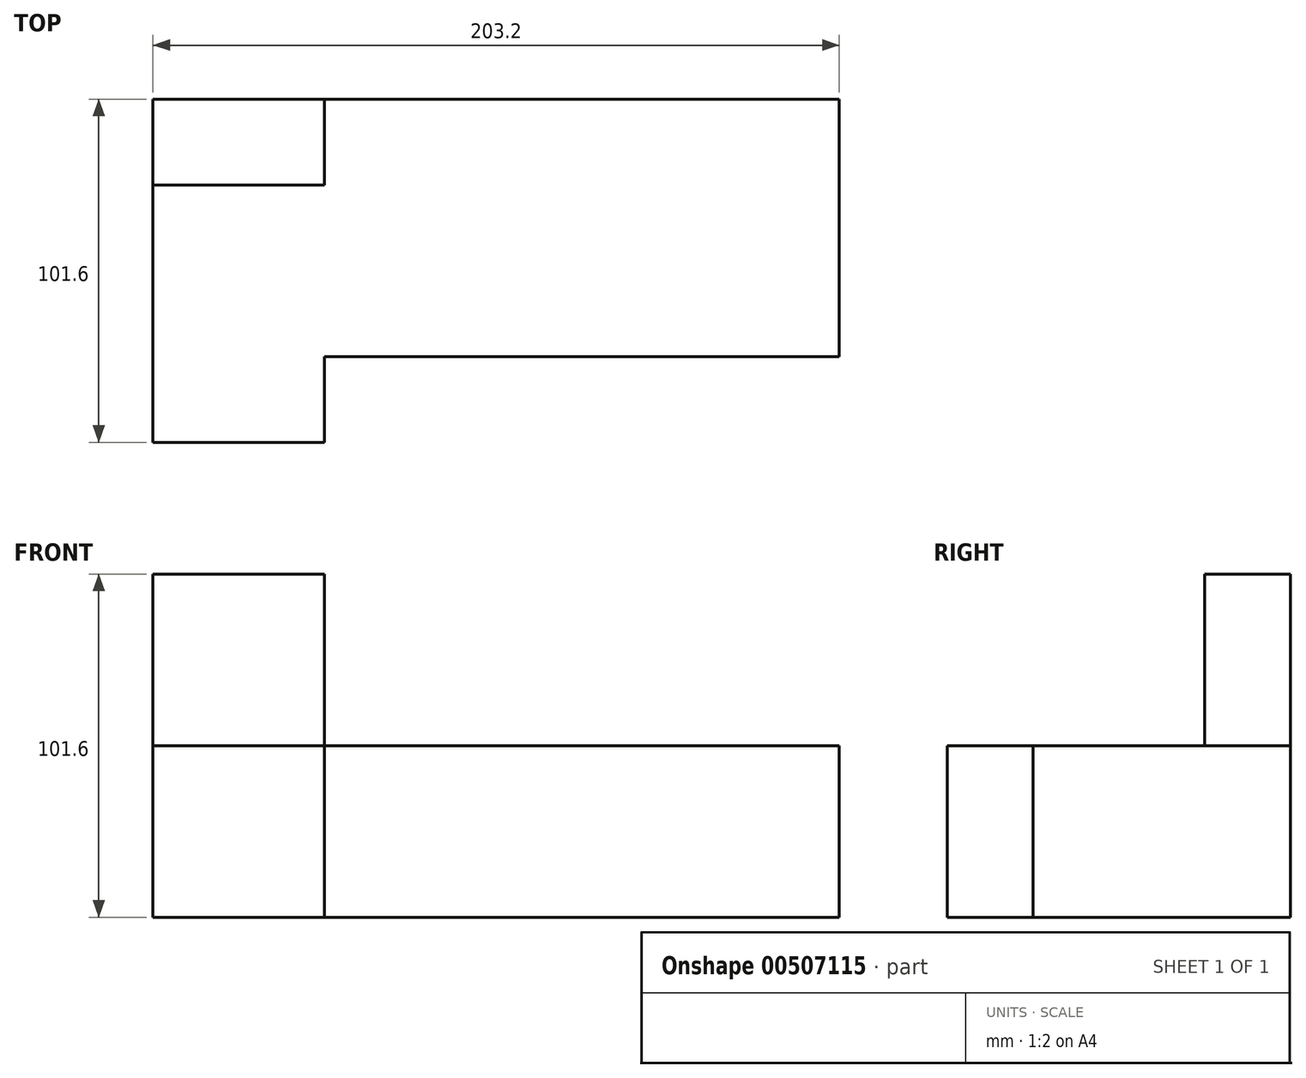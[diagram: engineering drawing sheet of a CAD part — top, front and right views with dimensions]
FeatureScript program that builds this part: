
annotation { "Feature Type Name" : "Feature", "Feature Type Description" : "" }
export const myFeature = defineFeature(function(context is Context, id is Id, definition is map)
    precondition{}
    {
        {
            var Q0;
            Q0=qCreatedBy(makeId("Top.planeOp"),FACE);
            var sketch = newSketch(context, id + "F0", { "sketchPlane" : qUnion([Q0])});
            skLineSegment(sketch, "E0.bottom", {"start": v(101.6, 50.8) * mm, "end": v(-101.6, 50.8) * mm});
            skLineSegment(sketch, "E0.top", {"start": v(101.6, -50.8) * mm, "end": v(-101.6, -50.8) * mm});
            skLineSegment(sketch, "E0.left", {"start": v(101.6, 50.8) * mm, "end": v(101.6, -50.8) * mm});
            skLineSegment(sketch, "E0.right", {"start": v(-101.6, 50.8) * mm, "end": v(-101.6, -50.8) * mm});
            skPoint(sketch, "E0.middle", {"position": v(0, 0) * mm});
            skSolve(sketch);
        }
        {
            var Q0;
            Q0 = qSketchRegion(id + "F0", true);
            extrude(context, id + "F1", {"entities" : qUnion([Q0]), "depth" : 50.8 * mm});
        }
        {
            var Q0;
            Q0=makeQuery(id+"F1.opExtrude","CAP_FACE",FACE,{"disambiguationData":[OSD([sQuery(id+"F0.wireOp",EDGE,"E0.bottom"),sQuery(id+"F0.wireOp",EDGE,"E0.top"),sQuery(id+"F0.wireOp",EDGE,"E0.left"),sQuery(id+"F0.wireOp",EDGE,"E0.right")])],"isStart":false});
            var sketch = newSketch(context, id + "F2", { "sketchPlane" : qUnion([Q0])});
            skLineSegment(sketch, "E1.bottom", {"start": v(101.6, -50.8) * mm, "end": v(-50.8, -50.8) * mm});
            skLineSegment(sketch, "E1.top", {"start": v(101.6, -25.4) * mm, "end": v(-50.8, -25.4) * mm});
            skLineSegment(sketch, "E1.left", {"start": v(101.6, -50.8) * mm, "end": v(101.6, -25.4) * mm});
            skLineSegment(sketch, "E1.right", {"start": v(-50.8, -50.8) * mm, "end": v(-50.8, -25.4) * mm});
            skSolve(sketch);
        }
        {
            var Q0;
            Q0 = qSketchRegion(id + "F2", true);
            var Q1;
            Q1=makeQuery(id+"F2.imprint","IMPRINT",FACE,{"disambiguationData":[TD([[makeQuery(id+"F2.imprint","IMPRINT",EDGE,{"derivedFrom":sQuery(id+"F2.wireOp",EDGE,"E1.bottom")}),-1.0]])]});
            extrude(context, id + "F3", {"entities" : qUnion([Q0, Q1]), "operationType" : NewBodyOperationType.REMOVE, "oppositeDirection" : true, "depth" : 50.8 * mm});
        }
        {
            var Q0;
            Q0=makeQuery(id+"F1.opExtrude","CAP_FACE",FACE,{"disambiguationData":[OSD([sQuery(id+"F0.wireOp",EDGE,"E0.bottom"),sQuery(id+"F0.wireOp",EDGE,"E0.top"),sQuery(id+"F0.wireOp",EDGE,"E0.left"),sQuery(id+"F0.wireOp",EDGE,"E0.right")])],"isStart":false});
            var sketch = newSketch(context, id + "F4", { "sketchPlane" : qUnion([Q0])});
            skLineSegment(sketch, "E2.bottom", {"start": v(-101.6, 50.8) * mm, "end": v(-50.8, 50.8) * mm});
            skLineSegment(sketch, "E2.top", {"start": v(-101.6, 25.4) * mm, "end": v(-50.8, 25.4) * mm});
            skLineSegment(sketch, "E2.left", {"start": v(-101.6, 50.8) * mm, "end": v(-101.6, 25.4) * mm});
            skLineSegment(sketch, "E2.right", {"start": v(-50.8, 50.8) * mm, "end": v(-50.8, 25.4) * mm});
            skSolve(sketch);
        }
        {
            var Q0;
            Q0 = qSketchRegion(id + "F4", true);
            extrude(context, id + "F5", {"entities" : qUnion([Q0]), "operationType" : NewBodyOperationType.ADD, "depth" : 50.8 * mm});
        }
    });
